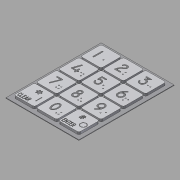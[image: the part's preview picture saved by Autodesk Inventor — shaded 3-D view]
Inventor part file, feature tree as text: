
AUTODESK INVENTOR PART (.ipt)
format: ipt  version: 2014 SP2 (Build 180246200, 246)  size: 1,493,504 bytes
history: native  units: mm
features: sketch x8, extrude x5, other x4, pattern_linear x3, projected_geometry x3, fillet x2
ambient origin geometry x8: Origin, YZ Plane, XZ Plane, XY Plane, X Axis, Y Axis, Z Axis, Center Point
bodies: Body1 (feature_tree)
feature tree (25):
  other  "Těleso1"
  extrude  "Vysunutí1"  Depth=53.0mm
  extrude  "Vysunutí2"  Depth=71.0mm
  pattern_linear  "Obdélníkové pole1"  Spacing1=0.5mm  [1 undecoded]
  sketch  "Náčrt6"
  extrude  "Vysunutí3"  Depth=17.0mm
  other  "Reliéf2"
  sketch  "Náčrt8"
  other  "Pracovní rovina1"
  other  "Rotace1"
  pattern_linear  "Obdélníkové pole2"  Spacing1=17.0mm  [1 undecoded]
  pattern_linear  "Obdélníkové pole3"  Spacing1=16.6mm  [1 undecoded]
  extrude  "Vysunutí4"  Depth=16.6mm
  extrude  "Vysunutí5"  Depth=0.2mm
  fillet  "Zaoblení1"  Radius=0.2mm
  fillet  "Zaoblení2"  Radius=30.0mm
  sketch  "Náčrt4"
  sketch  "Náčrt5"
  projected_geometry  "Promítnutá smyčka1"
  sketch  "Náčrt7"
  projected_geometry  "Promítnutá smyčka2"
  projected_geometry  "Promítnutá smyčka3"
  sketch  "Náčrt9"
  sketch  "Náčrt16"
  sketch  "Náčrt17"
note: 3 required parameter values undecoded (feature->parameter linkage not recoverable at this tier; creation-order binding heuristic only, values carry confidence <= 0.55)
